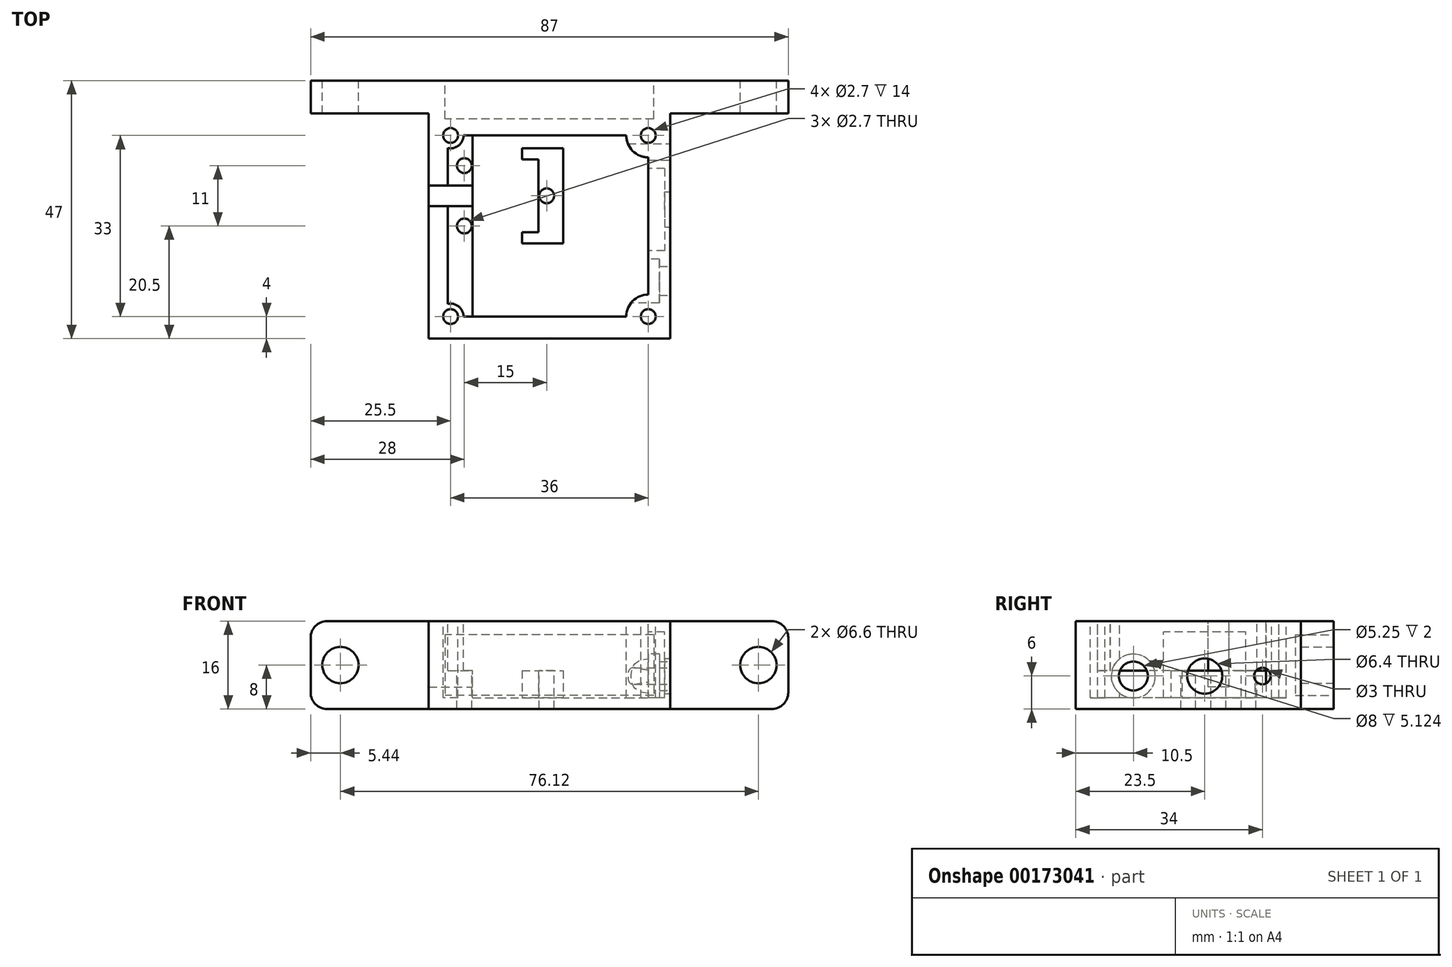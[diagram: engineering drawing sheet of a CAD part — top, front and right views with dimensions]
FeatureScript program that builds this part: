
annotation { "Feature Type Name" : "Feature", "Feature Type Description" : "" }
export const myFeature = defineFeature(function(context is Context, id is Id, definition is map)
    precondition{}
    {
        {
            var Q0;
            Q0=qCreatedBy(makeId("Top.planeOp"),FACE);
            var sketch = newSketch(context, id + "F0", { "sketchPlane" : qUnion([Q0])});
            skLineSegment(sketch, "E0.bottom", {"start": v(-22, 20.5) * mm, "end": v(22, 20.5) * mm});
            skLineSegment(sketch, "E0.top", {"start": v(-22, -20.5) * mm, "end": v(22, -20.5) * mm});
            skLineSegment(sketch, "E0.left", {"start": v(-22, 20.5) * mm, "end": v(-22, -20.5) * mm});
            skLineSegment(sketch, "E0.right", {"start": v(22, 20.5) * mm, "end": v(22, -20.5) * mm});
            skSolve(sketch);
        }
        {
            var Q0;
            Q0 = qSketchRegion(id + "F0", true);
            extrude(context, id + "F1", {"entities" : qUnion([Q0]), "depth" : 16 * mm});
        }
        {
            var Q0;
            Q0=makeQuery(id+"F1.opExtrude","CAP_FACE",FACE,{"disambiguationData":[OSD([sQuery(id+"F0.wireOp",EDGE,"E0.bottom"),sQuery(id+"F0.wireOp",EDGE,"E0.top"),sQuery(id+"F0.wireOp",EDGE,"E0.left"),sQuery(id+"F0.wireOp",EDGE,"E0.right")])],"isStart":false});
            var sketch = newSketch(context, id + "F2", { "sketchPlane" : qUnion([Q0])});
            skLineSegment(sketch, "E1.1", {"start": v(-14, 16.5) * mm, "end": v(14, 16.5) * mm});
            skLineSegment(sketch, "E1.2", {"start": v(18, 12.5) * mm, "end": v(18, -12.5) * mm});
            skLineSegment(sketch, "E1.3", {"start": v(-14, -16.5) * mm, "end": v(14, -16.5) * mm});
            skArc(sketch, "E2", {"start": v(14, 16.5) * mm, "mid": v(15.17, 13.67) * mm, "end": v(18, 12.5) * mm});
            skArc(sketch, "E3", {"start": v(18, -12.5) * mm, "mid": v(15.17, -13.67) * mm, "end": v(14, -16.5) * mm});
            skCircle(sketch, "E4", {"center": v(-18, 16.5) * mm, "radius": 1.35 * mm});
            skCircle(sketch, "E5", {"center": v(18, 16.5) * mm, "radius": 1.35 * mm});
            skCircle(sketch, "E6", {"center": v(-18, -16.5) * mm, "radius": 1.35 * mm});
            skCircle(sketch, "E7", {"center": v(18, -16.5) * mm, "radius": 1.35 * mm});
            skLineSegment(sketch, "E8", {"start": v(-14, 16.5) * mm, "end": v(-14, -16.5) * mm});
            skSolve(sketch);
        }
        {
            var Q0;
            Q0 = qSketchRegion(id + "F2", true);
            extrude(context, id + "F3", {"entities" : qUnion([Q0]), "operationType" : NewBodyOperationType.REMOVE, "oppositeDirection" : true, "depth" : 14 * mm});
        }
        {
            var Q0;
            Q0=qCreatedBy(makeId("Top.planeOp"),FACE);
            var sketch = newSketch(context, id + "F4", { "sketchPlane" : qUnion([Q0])});
            skLineSegment(sketch, "E9.bottom", {"start": v(-14, 12.15) * mm, "end": v(-2, 12.15) * mm, "construction": true});
            skLineSegment(sketch, "E9.top", {"start": v(-14, -1.15) * mm, "end": v(-2, -1.15) * mm, "construction": true});
            skLineSegment(sketch, "E9.left", {"start": v(-14, 12.15) * mm, "end": v(-14, -1.15) * mm, "construction": true});
            skLineSegment(sketch, "E9.right", {"start": v(-2, 12.15) * mm, "end": v(-2, -1.15) * mm, "construction": true});
            skLineSegment(sketch, "E10", {"start": v(-18.5, 17.4) * mm, "end": v(-18.5, -21.08) * mm, "construction": true});
            skLineSegment(sketch, "E11", {"start": v(-15.5, 19.24) * mm, "end": v(-15.5, -21.46) * mm, "construction": true});
            skLineSegment(sketch, "E12.bottom", {"start": v(-5, -3.15) * mm, "end": v(2.5, -3.15) * mm});
            skLineSegment(sketch, "E12.top", {"start": v(-5, 14.15) * mm, "end": v(2.5, 14.15) * mm});
            skLineSegment(sketch, "E12.left", {"start": v(-5, -3.15) * mm, "end": v(-5, -1.15) * mm});
            skLineSegment(sketch, "E12.right", {"start": v(2.5, -3.15) * mm, "end": v(2.5, 14.15) * mm});
            skLineSegment(sketch, "E13", {"start": v(-5, 12.15) * mm, "end": v(-2, 12.15) * mm});
            skLineSegment(sketch, "E14", {"start": v(-2, -1.15) * mm, "end": v(-5, -1.15) * mm});
            skLineSegment(sketch, "E15.trimOffspring", {"start": v(-5, 12.15) * mm, "end": v(-5, 14.15) * mm});
            skLineSegment(sketch, "E16", {"start": v(-2, 12.15) * mm, "end": v(-2, -1.15) * mm});
            skSolve(sketch);
        }
        {
            var Q0;
            Q0=makeQuery(id+"F1.opExtrude","CAP_FACE",FACE,{"disambiguationData":[OSD([sQuery(id+"F0.wireOp",EDGE,"E0.bottom"),sQuery(id+"F0.wireOp",EDGE,"E0.top"),sQuery(id+"F0.wireOp",EDGE,"E0.left"),sQuery(id+"F0.wireOp",EDGE,"E0.right")])],"isStart":false});
            var sketch = newSketch(context, id + "F5", { "sketchPlane" : qUnion([Q0])});
            skArc(sketch, "E17.0", {"start": v(-18.5, 14.2) * mm, "mid": v(-16.53, 14.67) * mm, "end": v(-15.65, 16.5) * mm});
            skLineSegment(sketch, "E18", {"start": v(-14, 16.5) * mm, "end": v(-15.65, 16.5) * mm});
            skLineSegment(sketch, "E19", {"start": v(-18.5, 14.2) * mm, "end": v(-18.5, -14.2) * mm});
            skArc(sketch, "E20.0", {"start": v(-15.65, -16.5) * mm, "mid": v(-16.53, -14.67) * mm, "end": v(-18.5, -14.2) * mm});
            skLineSegment(sketch, "E21", {"start": v(-14, -16.5) * mm, "end": v(-15.65, -16.5) * mm});
            skLineSegment(sketch, "E22", {"start": v(-14, -16.5) * mm, "end": v(-14, 16.5) * mm});
            skSolve(sketch);
        }
        {
            var Q0;
            Q0 = qSketchRegion(id + "F5", true);
            extrude(context, id + "F6", {"entities" : qUnion([Q0]), "operationType" : NewBodyOperationType.REMOVE, "oppositeDirection" : true, "depth" : 9 * mm});
        }
        {
            var Q0;
            Q0 = qSketchRegion(id + "F4", true);
            extrude(context, id + "F7", {"entities" : qUnion([Q0]), "operationType" : NewBodyOperationType.ADD, "depth" : 7 * mm});
        }
        {
            var Q0;
            Q0=makeQuery(id+"F7.opExtrude","CAP_FACE",FACE,{"disambiguationData":[OSD([sQuery(id+"F4.wireOp",EDGE,"E12.bottom"),sQuery(id+"F4.wireOp",EDGE,"E12.top"),sQuery(id+"F4.wireOp",EDGE,"E12.left"),sQuery(id+"F4.wireOp",EDGE,"E12.right"),sQuery(id+"F4.wireOp",EDGE,"E13"),sQuery(id+"F4.wireOp",EDGE,"E14"),sQuery(id+"F4.wireOp",EDGE,"E15.trimOffspring"),sQuery(id+"F4.wireOp",EDGE,"E16")])],"isStart":false});
            var sketch = newSketch(context, id + "F8", { "sketchPlane" : qUnion([Q0])});
            skLineSegment(sketch, "E23", {"start": v(-20.4, 5.5) * mm, "end": v(19.57, 5.5) * mm, "construction": true});
            skLineSegment(sketch, "E24", {"start": v(-15.5, 19.05) * mm, "end": v(-15.5, -8.25) * mm, "construction": true});
            skCircle(sketch, "E25", {"center": v(-0.5, 5.5) * mm, "radius": 1.35 * mm});
            skCircle(sketch, "E26", {"center": v(-15.5, 11) * mm, "radius": 1.35 * mm});
            skCircle(sketch, "E27", {"center": v(-15.5, 0) * mm, "radius": 1.35 * mm});
            skSolve(sketch);
        }
        {
            var Q0;
            Q0 = qSketchRegion(id + "F8", true);
            extrude(context, id + "F9", {"entities" : qUnion([Q0]), "operationType" : NewBodyOperationType.REMOVE, "endBound" : BoundingType.THROUGH_ALL, "oppositeDirection" : true, "depth" : 25 * mm});
        }
        {
            var Q0;
            Q0=makeQuery(id+"F3.boolean.opBoolean","COPY",FACE,{"derivedFrom":makeQuery(id+"F3.opExtrude","CAP_FACE",FACE,{"disambiguationData":[OSD([sQuery(id+"F2.wireOp",EDGE,"E1.1"),sQuery(id+"F2.wireOp",EDGE,"E1.2"),sQuery(id+"F2.wireOp",EDGE,"E1.3"),sQuery(id+"F2.wireOp",EDGE,"E2"),sQuery(id+"F2.wireOp",EDGE,"E3"),sQuery(id+"F2.wireOp",EDGE,"E8")])],"isStart":false})});
            var sketch = newSketch(context, id + "F10", { "sketchPlane" : qUnion([Q0])});
            skLineSegment(sketch, "E28.bottom", {"start": v(18, 9.5) * mm, "end": v(4.5, 9.5) * mm, "construction": true});
            skLineSegment(sketch, "E28.top", {"start": v(18, -3.5) * mm, "end": v(4.5, -3.5) * mm, "construction": true});
            skLineSegment(sketch, "E28.left", {"start": v(18, 9.5) * mm, "end": v(18, -3.5) * mm, "construction": true});
            skLineSegment(sketch, "E28.right", {"start": v(4.5, 9.5) * mm, "end": v(4.5, -3.5) * mm, "construction": true});
            skLineSegment(sketch, "E29.bottom", {"start": v(-10.48, -8.77) * mm, "end": v(10.52, -8.77) * mm, "construction": true});
            skLineSegment(sketch, "E29.top", {"start": v(-10.48, -15.27) * mm, "end": v(10.52, -15.27) * mm, "construction": true});
            skLineSegment(sketch, "E29.left", {"start": v(-10.48, -8.77) * mm, "end": v(-10.48, -15.27) * mm, "construction": true});
            skLineSegment(sketch, "E29.right", {"start": v(10.52, -8.77) * mm, "end": v(10.52, -15.27) * mm, "construction": true});
            skSolve(sketch);
        }
        {
            var Q0;
            Q0=makeQuery(id+"F1.opExtrude","SWEPT_FACE",FACE,{"disambiguationData":[OSD([sQuery(id+"F0.wireOp",EDGE,"E0.right")])]});
            var sketch = newSketch(context, id + "F11", { "sketchPlane" : qUnion([Q0])});
            skCircle(sketch, "E30", {"center": v(3, 6) * mm, "radius": 3.2 * mm});
            skCircle(sketch, "E31", {"center": v(13.5, 6) * mm, "radius": 1.5 * mm});
            skLineSegment(sketch, "E32", {"start": v(-25.27, 6) * mm, "end": v(30.9, 6) * mm, "construction": true});
            skCircle(sketch, "E33", {"center": v(-10, 6) * mm, "radius": 2.62 * mm});
            skSolve(sketch);
        }
        {
            var Q0;
            Q0 = qSketchRegion(id + "F11", true);
            extrude(context, id + "F12", {"entities" : qUnion([Q0]), "operationType" : NewBodyOperationType.REMOVE, "oppositeDirection" : true, "depth" : 10 * mm});
        }
        {
            var Q0;
            Q0=makeQuery(id+"F1.opExtrude","CAP_FACE",FACE,{"disambiguationData":[OSD([sQuery(id+"F0.wireOp",EDGE,"E0.bottom"),sQuery(id+"F0.wireOp",EDGE,"E0.top"),sQuery(id+"F0.wireOp",EDGE,"E0.left"),sQuery(id+"F0.wireOp",EDGE,"E0.right")])],"isStart":false});
            var sketch = newSketch(context, id + "F13", { "sketchPlane" : qUnion([Q0])});
            skLineSegment(sketch, "E34", {"start": v(-32.73, 5.5) * mm, "end": v(10.98, 5.5) * mm, "construction": true});
            skLineSegment(sketch, "E35.bottom", {"start": v(-22, 7.4) * mm, "end": v(-14, 7.4) * mm});
            skLineSegment(sketch, "E35.top", {"start": v(-22, 3.6) * mm, "end": v(-14, 3.6) * mm});
            skLineSegment(sketch, "E35.left", {"start": v(-22, 7.4) * mm, "end": v(-22, 3.6) * mm});
            skLineSegment(sketch, "E35.right", {"start": v(-14, 7.4) * mm, "end": v(-14, 3.6) * mm});
            skSolve(sketch);
        }
        {
            var Q0;
            Q0 = qSketchRegion(id + "F13", true);
            extrude(context, id + "F14", {"entities" : qUnion([Q0]), "operationType" : NewBodyOperationType.REMOVE, "oppositeDirection" : true, "depth" : 12 * mm});
        }
        {
            var Q0;
            Q0=makeQuery(id+"F1.opExtrude","SWEPT_FACE",FACE,{"disambiguationData":[OSD([sQuery(id+"F0.wireOp",EDGE,"E0.bottom")])]});
            var sketch = newSketch(context, id + "F15", { "sketchPlane" : qUnion([Q0])});
            skLineSegment(sketch, "E36.bottom", {"start": v(43.5, 0) * mm, "end": v(-43.5, 0) * mm});
            skLineSegment(sketch, "E36.top", {"start": v(43.5, 16) * mm, "end": v(-43.5, 16) * mm});
            skLineSegment(sketch, "E36.left", {"start": v(43.5, 0) * mm, "end": v(43.5, 16) * mm});
            skLineSegment(sketch, "E36.right", {"start": v(-43.5, 0) * mm, "end": v(-43.5, 16) * mm});
            skSolve(sketch);
        }
        {
            var Q0;
            Q0 = qSketchRegion(id + "F15", true);
            extrude(context, id + "F16", {"entities" : qUnion([Q0]), "operationType" : NewBodyOperationType.ADD, "depth" : 6 * mm});
        }
        {
            var Q0;
            Q0=makeQuery(id+"F16.opExtrude","CAP_FACE",FACE,{"disambiguationData":[OSD([sQuery(id+"F15.wireOp",EDGE,"E36.bottom"),sQuery(id+"F15.wireOp",EDGE,"E36.top"),sQuery(id+"F15.wireOp",EDGE,"E36.left"),sQuery(id+"F15.wireOp",EDGE,"E36.right")])],"isStart":false});
            var sketch = newSketch(context, id + "F17", { "sketchPlane" : qUnion([Q0])});
            skLineSegment(sketch, "E37", {"start": v(47.23, 8) * mm, "end": v(-48.21, 8) * mm, "construction": true});
            skPoint(sketch, "E37.startSnap0", {"position": v(43.5, 8) * mm});
            skCircle(sketch, "E38", {"center": v(38.06, 8) * mm, "radius": 3.3 * mm});
            skCircle(sketch, "E39", {"center": v(-38.06, 8) * mm, "radius": 3.3 * mm});
            skSolve(sketch);
        }
        {
            var Q0;
            Q0 = qSketchRegion(id + "F17", true);
            extrude(context, id + "F18", {"entities" : qUnion([Q0]), "operationType" : NewBodyOperationType.REMOVE, "endBound" : BoundingType.THROUGH_ALL, "oppositeDirection" : true, "depth" : 25 * mm});
        }
        {
            var Q0;
            Q0=makeQuery(id+"F16.opExtrude","SWEPT_EDGE",EDGE,{"disambiguationData":[OSD([sQuery(id+"F15.wireOp",EDGE,"E36.top"),sQuery(id+"F15.wireOp",EDGE,"E36.right")])]});
            var Q1;
            Q1=makeQuery(id+"F16.opExtrude","SWEPT_EDGE",EDGE,{"disambiguationData":[OSD([sQuery(id+"F15.wireOp",EDGE,"E36.bottom"),sQuery(id+"F15.wireOp",EDGE,"E36.right")])]});
            var Q2;
            Q2=makeQuery(id+"F16.opExtrude","SWEPT_EDGE",EDGE,{"disambiguationData":[OSD([sQuery(id+"F15.wireOp",EDGE,"E36.bottom"),sQuery(id+"F15.wireOp",EDGE,"E36.left")])]});
            var Q3;
            Q3=makeQuery(id+"F16.opExtrude","SWEPT_EDGE",EDGE,{"disambiguationData":[OSD([sQuery(id+"F15.wireOp",EDGE,"E36.top"),sQuery(id+"F15.wireOp",EDGE,"E36.left")])]});
            fillet(context, id + "F19", {"entities" : qUnion([Q0, Q1, Q2, Q3]), "radius" : 3 * mm, "tangentPropagation" : true, "allowEdgeOverflow" : false});
        }
        {
            var Q0;
            Q0=makeQuery(id+"F3.boolean.opBoolean","COPY",FACE,{"derivedFrom":makeQuery(id+"F3.opExtrude","SWEPT_FACE",FACE,{"disambiguationData":[OSD([sQuery(id+"F2.wireOp",EDGE,"E1.2")])]})});
            var sketch = newSketch(context, id + "F20", { "sketchPlane" : qUnion([Q0])});
            skLineSegment(sketch, "E40.bottom", {"start": v(-10.5, 2) * mm, "end": v(4.5, 2) * mm});
            skLineSegment(sketch, "E40.top", {"start": v(-10.5, 14) * mm, "end": v(4.5, 14) * mm});
            skLineSegment(sketch, "E40.left", {"start": v(-10.5, 2) * mm, "end": v(-10.5, 14) * mm});
            skLineSegment(sketch, "E40.right", {"start": v(4.5, 2) * mm, "end": v(4.5, 14) * mm});
            skLineSegment(sketch, "E41", {"start": v(-3, 19.71) * mm, "end": v(-3, -2.98) * mm, "construction": true});
            skSolve(sketch);
        }
        {
            var Q0;
            Q0 = qSketchRegion(id + "F20", true);
            extrude(context, id + "F21", {"entities" : qUnion([Q0]), "operationType" : NewBodyOperationType.REMOVE, "oppositeDirection" : true, "depth" : 3 * mm});
        }
        {
            var Q0;
            Q0=makeQuery(id+"F16.opExtrude","CAP_FACE",FACE,{"disambiguationData":[OSD([sQuery(id+"F15.wireOp",EDGE,"E36.bottom"),sQuery(id+"F15.wireOp",EDGE,"E36.top"),sQuery(id+"F15.wireOp",EDGE,"E36.left"),sQuery(id+"F15.wireOp",EDGE,"E36.right")])],"isStart":false});
            var sketch = newSketch(context, id + "F22", { "sketchPlane" : qUnion([Q0])});
            skLineSegment(sketch, "E42.bottom", {"start": v(-19, 13.5) * mm, "end": v(19, 13.5) * mm});
            skLineSegment(sketch, "E42.top", {"start": v(-19, 2.5) * mm, "end": v(19, 2.5) * mm});
            skLineSegment(sketch, "E42.left", {"start": v(-19, 13.5) * mm, "end": v(-19, 2.5) * mm});
            skLineSegment(sketch, "E42.right", {"start": v(19, 13.5) * mm, "end": v(19, 2.5) * mm});
            skLineSegment(sketch, "E43", {"start": v(-47.87, 8) * mm, "end": v(51.75, 8) * mm, "construction": true});
            skPoint(sketch, "E43.startSnap0", {"position": v(-43.5, 8) * mm});
            skPoint(sketch, "E43.endSnap0", {"position": v(43.5, 8) * mm});
            skSolve(sketch);
        }
        {
            var Q0;
            Q0 = qSketchRegion(id + "F22", true);
            extrude(context, id + "F23", {"entities" : qUnion([Q0]), "operationType" : NewBodyOperationType.REMOVE, "oppositeDirection" : true, "depth" : 7 * mm});
        }
        {
            var Q0;
            Q0=makeQuery(id+"F3.boolean.opBoolean","COPY",FACE,{"derivedFrom":makeQuery(id+"F3.opExtrude","SWEPT_FACE",FACE,{"disambiguationData":[OSD([sQuery(id+"F2.wireOp",EDGE,"E1.2")])]})});
            cPlane(context, id + "F24", {"entities" : qUnion([Q0]), "cplaneType" : CPlaneType.OFFSET, "offset" : 5 * mm, "width" : 150 * mm, "height" : 150 * mm});
        }
        {
            var Q0;
            Q0=qCreatedBy(id+"F24.planeOp",FACE);
            var sketch = newSketch(context, id + "F25", { "sketchPlane" : qUnion([Q0])});
            skCircle(sketch, "E44", {"center": v(10, 6) * mm, "radius": 4 * mm});
            skSolve(sketch);
        }
        {
            var Q0;
            Q0 = qSketchRegion(id + "F25", true);
            extrude(context, id + "F26", {"entities" : qUnion([Q0]), "operationType" : NewBodyOperationType.REMOVE, "oppositeDirection" : true, "depth" : 7 * mm});
        }
    });
